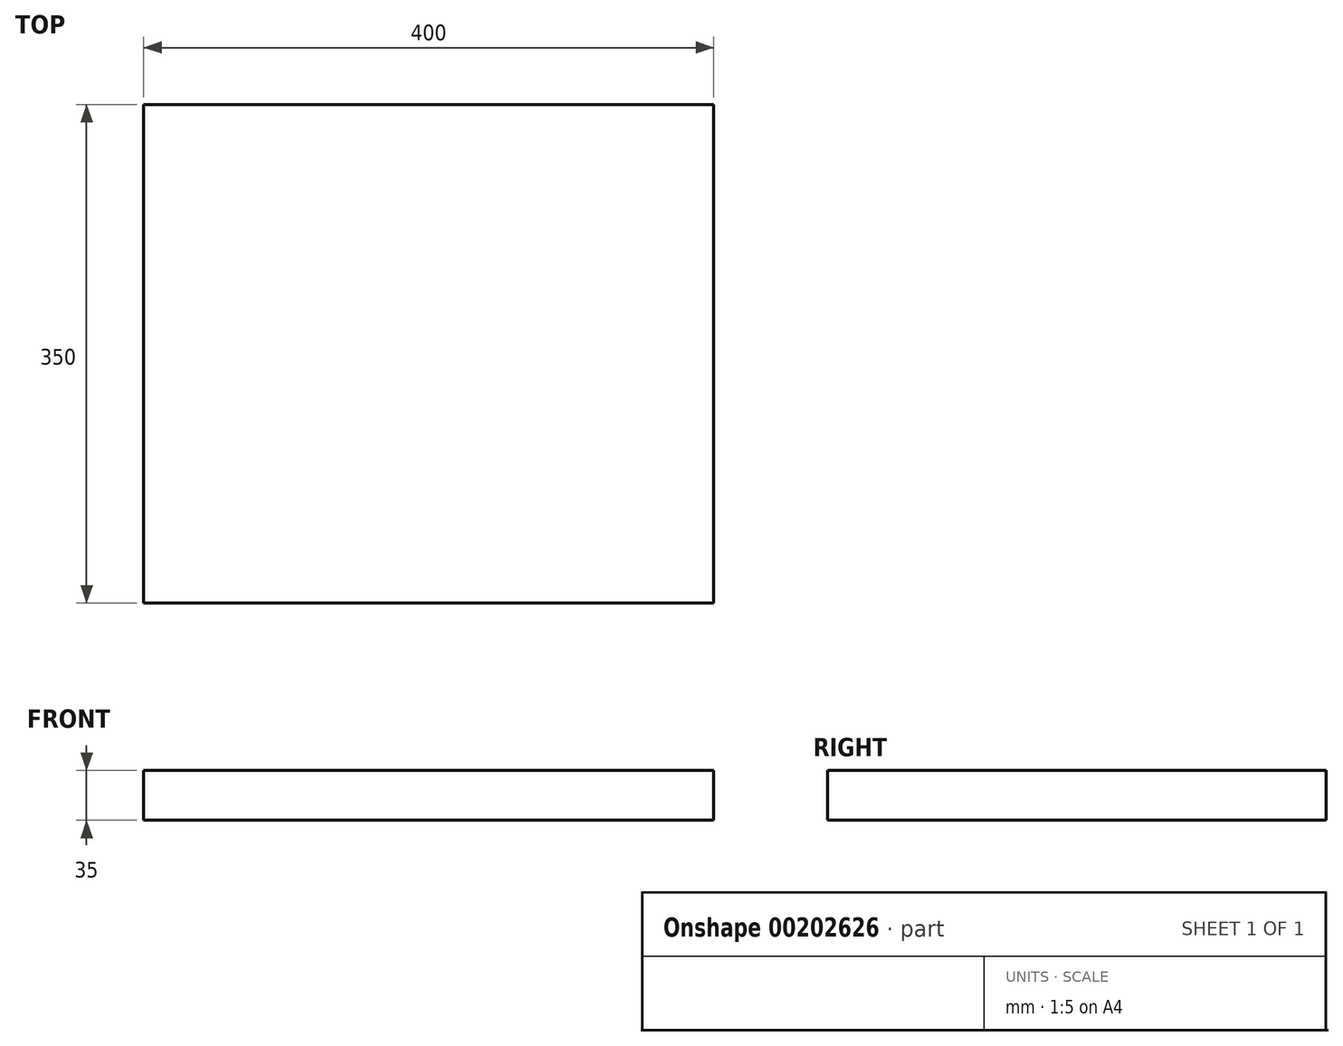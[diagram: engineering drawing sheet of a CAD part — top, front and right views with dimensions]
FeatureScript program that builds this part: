
annotation { "Feature Type Name" : "Feature", "Feature Type Description" : "" }
export const myFeature = defineFeature(function(context is Context, id is Id, definition is map)
    precondition{}
    {
        {
            var Q0;
            Q0=qCreatedBy(makeId("Top.planeOp"),FACE);
            var sketch = newSketch(context, id + "F0", { "sketchPlane" : qUnion([Q0])});
            skLineSegment(sketch, "E0.bottom", {"start": v(-864.34, -235.28) * mm, "end": v(-464.34, -235.28) * mm});
            skLineSegment(sketch, "E0.top", {"start": v(-864.34, 114.72) * mm, "end": v(-464.34, 114.72) * mm});
            skLineSegment(sketch, "E0.left", {"start": v(-864.34, -235.28) * mm, "end": v(-864.34, 114.72) * mm});
            skLineSegment(sketch, "E0.right", {"start": v(-464.34, -235.28) * mm, "end": v(-464.34, 114.72) * mm});
            skSolve(sketch);
        }
        {
            var Q0;
            Q0=makeQuery(id+"F0.imprint","IMPRINT",FACE,{"disambiguationData":[TD([[makeQuery(id+"F0.imprint","IMPRINT",EDGE,{"derivedFrom":sQuery(id+"F0.wireOp",EDGE,"E0.bottom")}),1.0]])]});
            extrude(context, id + "F1", {"entities" : qUnion([Q0]), "depth" : 35 * mm});
        }
    });
